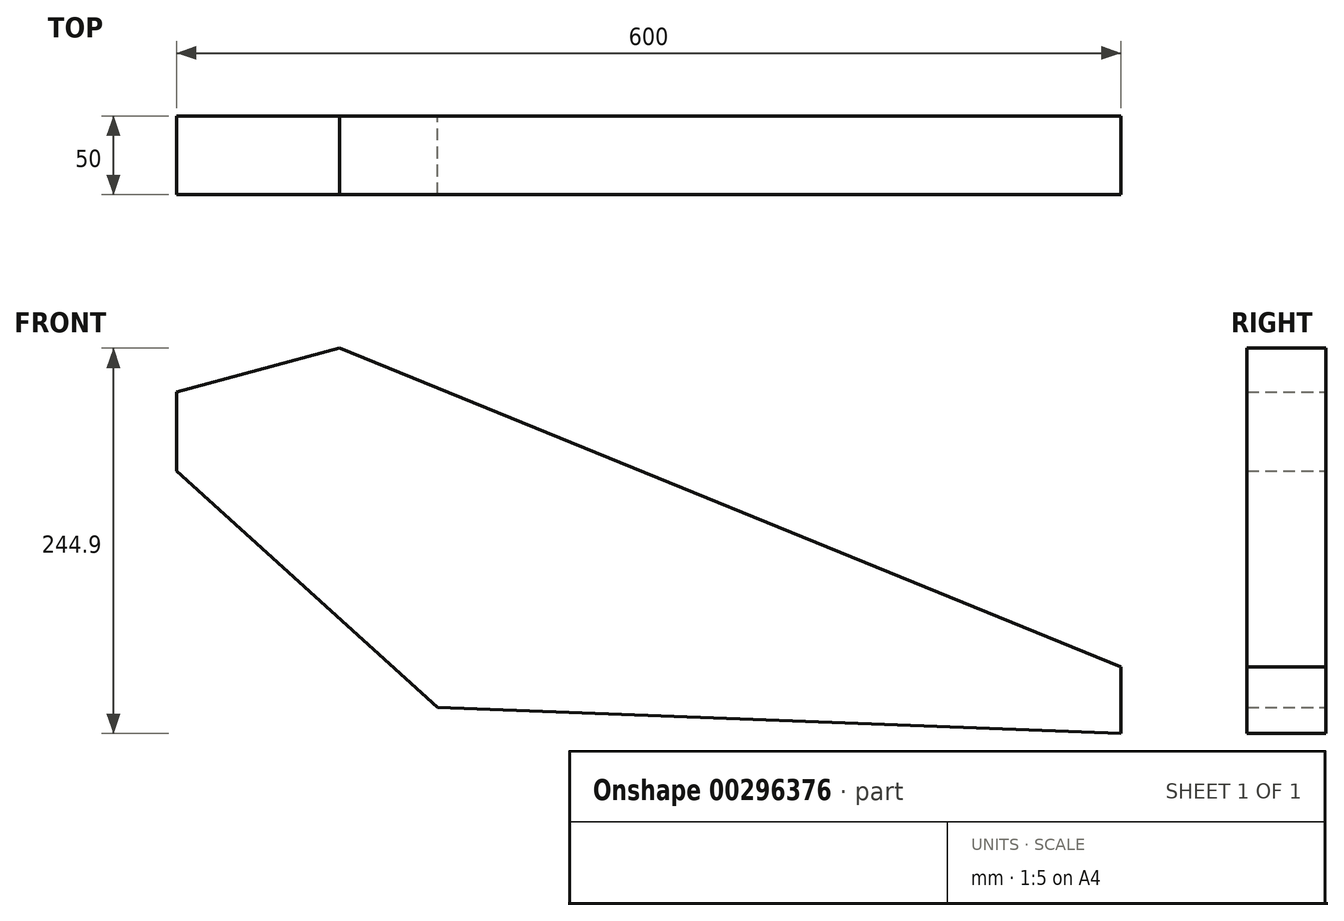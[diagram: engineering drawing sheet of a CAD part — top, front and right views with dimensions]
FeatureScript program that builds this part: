
annotation { "Feature Type Name" : "Feature", "Feature Type Description" : "" }
export const myFeature = defineFeature(function(context is Context, id is Id, definition is map)
    precondition{}
    {
        {
            var Q0;
            Q0=qCreatedBy(makeId("Front.planeOp"),FACE);
            var sketch = newSketch(context, id + "F0", { "sketchPlane" : qUnion([Q0])});
            skLineSegment(sketch, "E0", {"start": v(-318.76, 21.78) * mm, "end": v(-318.76, 71.87) * mm});
            skLineSegment(sketch, "E1", {"start": v(-318.76, 71.87) * mm, "end": v(-215.24, 99.7) * mm});
            skLineSegment(sketch, "E2", {"start": v(-215.24, 99.7) * mm, "end": v(281.24, -102.9) * mm});
            skLineSegment(sketch, "E3", {"start": v(281.24, -102.9) * mm, "end": v(281.24, -145.2) * mm});
            skLineSegment(sketch, "E4", {"start": v(281.24, -145.2) * mm, "end": v(-152.9, -128.5) * mm});
            skLineSegment(sketch, "E5", {"start": v(-152.9, -128.5) * mm, "end": v(-318.76, 21.78) * mm});
            skSolve(sketch);
        }
        {
            var Q0;
            Q0=makeQuery(id+"F0.imprint","IMPRINT",FACE,{"disambiguationData":[TD([[makeQuery(id+"F0.imprint","IMPRINT",EDGE,{"derivedFrom":sQuery(id+"F0.wireOp",EDGE,"E0")}),-1.0]])]});
            extrude(context, id + "F1", {"entities" : qUnion([Q0]), "depth" : 50 * mm});
        }
    });
